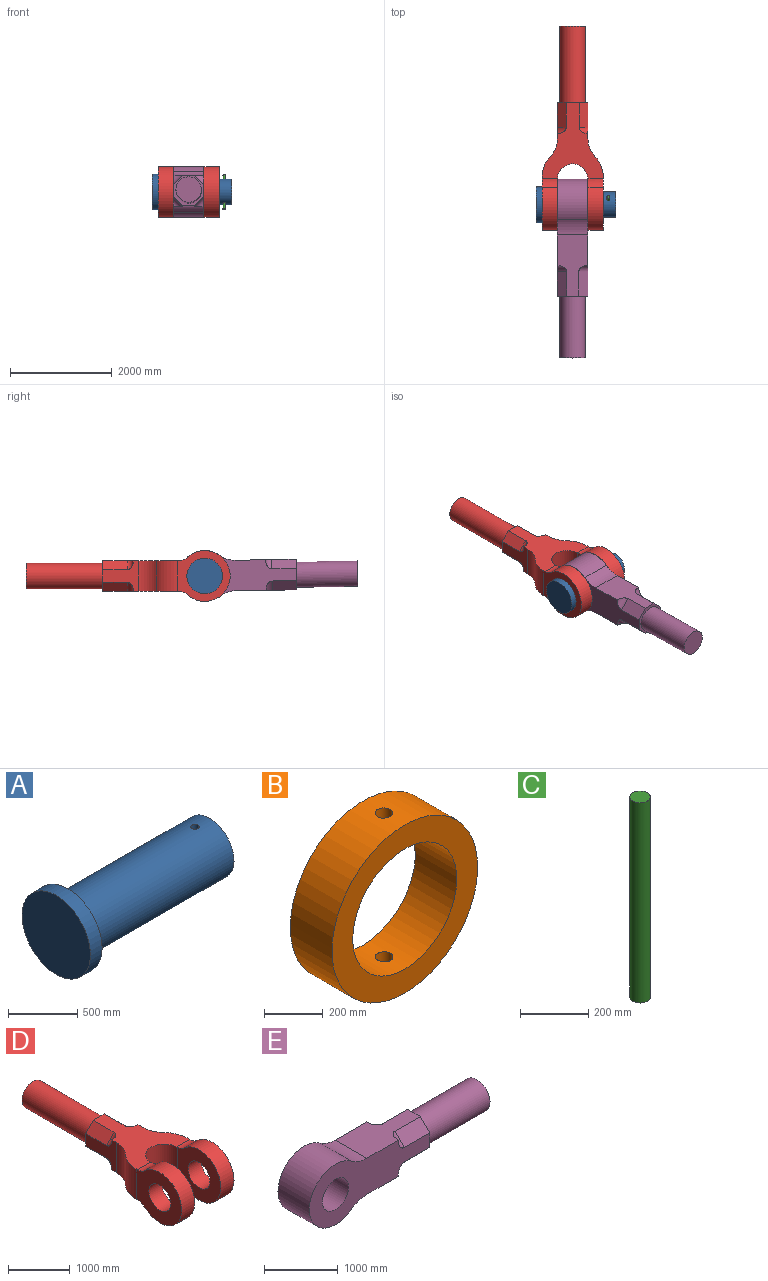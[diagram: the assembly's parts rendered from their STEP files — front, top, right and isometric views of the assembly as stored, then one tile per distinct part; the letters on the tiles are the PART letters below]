
ASSEMBLY  parts=5 mates=5
PART A: 6 faces, bbox 1570x700x700 mm
  f0: cylinder r=250mm len=1450mm, axis (-1,0,0), area 2272006.1mm2, adj f1,f2,f5
  f1: plane 500x500mm, normal (1,0,0), area 196349.5mm2, adj f0
  f2: plane 700x700mm, normal (1,0,0), area 188495.6mm2, adj f0,f3
  f3: cylinder r=350mm len=700mm, axis (-1,0,0), area 263893.8mm2, adj f2,f4
  f4: plane 700x700mm, normal (-1,0,0), area 384845.1mm2, adj f3
  f5: cylinder r=30mm len=500mm, axis (0,0,-1), area 93907.4mm2, adj f0
PART B: 6 faces, bbox 700x200x700 mm
  f0: cylinder r=250mm len=500mm, axis (0,1,0), area 308511.8mm2, adj f2,f3,f4,f5
  f1: cylinder r=350mm len=700mm, axis (0,1,0), area 434178.1mm2, adj f2,f3,f4,f5
  f2: plane 700x700mm, normal (0,-1,0), area 188495.6mm2, adj f0,f1
  f3: plane 700x700mm, normal (0,1,0), area 188495.6mm2, adj f0,f1
  f4: cylinder r=30mm len=101.81mm, axis (0,0,1), area 18898.3mm2, adj f0,f1
  f5: cylinder r=30mm len=101.81mm, axis (0,0,1), area 18898.2mm2, adj f0,f1
PART C: 3 faces, bbox 60x60x720 mm
  f0: cylinder r=30mm len=720mm, axis (0,0,-1), area 135716.8mm2, adj f1,f2
  f1: plane 60x60mm, normal (0,0,1), area 2827.4mm2, adj f0
  f2: plane 60x60mm, normal (0,0,-1), area 2827.4mm2, adj f0
PART D: 36 faces, bbox 1200x4007x1000 mm
  f0: plane 600x600mm, normal (0,1,0), area 103098.5mm2, adj f1,f2,f9,f18,f22,f24,f26,f28
  f1: plane 705.02x600mm, normal (-1,0,0), area 222950.5mm2, adj f0,f2,f7,f18,f24,f25,f26,f27
  f2: plane 1490.1x1200mm, normal (0,0,1), area 810833.6mm2, adj f0,f1,f3,f6,f7,f8,f9,f10
  f3: plane 1040x1000mm, normal (-1,0,0), area 635026.5mm2, adj f2,f6,f13,f15,f17,f18,f21
  f4: plane 1000x1000mm, normal (-1,0,0), area 611025.2mm2, adj f12,f14,f16,f19,f20
  f5: plane 1000x1000mm, normal (1,0,0), area 611025.2mm2, adj f12,f13,f15,f17,f21
  f6: cylinder r=600mm len=600mm, axis (0,0,1), area 272324.3mm2, adj f2,f3,f7,f18
  f7: cylinder r=500mm len=600mm, axis (0,0,1), area 226936.9mm2, adj f1,f2,f6,f18
  f8: cylinder r=600mm len=600mm, axis (0,0,1), area 272324.3mm2, adj f2,f10,f11,f18
  f9: plane 705.02x600mm, normal (1,0,0), area 222950.5mm2, adj f0,f2,f10,f18,f22,f23,f28,f29
  f10: cylinder r=500mm len=600mm, axis (0,0,1), area 226936.9mm2, adj f2,f8,f9,f18
  f11: plane 1040x1000mm, normal (1,0,0), area 635026.5mm2, adj f2,f8,f14,f16,f18,f19,f20
  f12: cylinder r=300mm len=600.39mm, axis (0,0,1), area 565489.3mm2, adj f2,f4,f5,f15,f16,f17,f18,f19
  f13: cylinder r=500mm len=1000mm, axis (1,0,0), area 695514.2mm2, adj f3,f5,f15,f17
  f14: cylinder r=500mm len=1000mm, axis (1,0,0), area 695514.2mm2, adj f4,f11,f16,f19
  f15: cylinder r=250mm len=300.16mm, axis (1,0,0), area 56069.4mm2, adj f2,f3,f5,f12,f13
  f16: cylinder r=250mm len=300.16mm, axis (1,0,0), area 56069.4mm2, adj f2,f4,f11,f12,f14
  f17: cylinder r=250mm len=300.16mm, axis (1,0,0), area 56069.4mm2, adj f3,f5,f12,f13,f18
  f18: plane 1490.1x1200mm, normal (0,0,-1), area 810833.6mm2, adj f0,f1,f3,f6,f7,f8,f9,f10
  f19: cylinder r=250mm len=300.16mm, axis (1,0,0), area 56069.4mm2, adj f4,f11,f12,f14,f18
  f20: cylinder r=250mm len=500mm, axis (1,0,0), area 471238.9mm2, adj f4,f11
  f21: cylinder r=250mm len=500mm, axis (1,0,0), area 471238.9mm2, adj f3,f5
  f22: plane 480x174mm, normal (0.71,0,-0.71), area 118115.1mm2, adj f0,f9,f18,f33
  f23: plane 4.29x4.29mm, normal (0,1,0), area 9.2mm2, adj f9,f18,f33
  f24: plane 480x174mm, normal (-0.71,0,-0.71), area 118115.1mm2, adj f0,f1,f18,f32
  f25: plane 4.29x4.29mm, normal (0,1,0), area 9.2mm2, adj f1,f18,f32
  f26: plane 480x174mm, normal (-0.71,0,0.71), area 118115.1mm2, adj f0,f1,f2,f35
  f27: plane 4.29x4.29mm, normal (0,1,0), area 9.2mm2, adj f1,f2,f35
  f28: plane 480x174mm, normal (0.71,0,0.71), area 118115.1mm2, adj f0,f2,f9,f34
  f29: plane 4.29x4.29mm, normal (0,1,0), area 9.2mm2, adj f2,f9,f34
  f30: cylinder r=250mm len=1507mm, axis (0,-1,0), area 2367190.1mm2, adj f0,f31
  f31: plane 500x500mm, normal (0,1,0), area 196349.5mm2, adj f30
  f32: cylinder r=120mm len=258.85mm, axis (0.71,0,-0.71), area 29944.8mm2, adj f1,f18,f24,f25
  f33: cylinder r=120mm len=258.85mm, axis (0.71,0,0.71), area 29944.8mm2, adj f9,f18,f22,f23
  f34: cylinder r=120mm len=258.85mm, axis (-0.71,0,0.71), area 29944.8mm2, adj f2,f9,f28,f29
  f35: cylinder r=120mm len=258.85mm, axis (-0.71,0,-0.71), area 29944.8mm2, adj f1,f2,f26,f27
PART E: 23 faces, bbox 3505x769.7x1000 mm
  f0: plane 1200x600mm, normal (0,0,1), area 512020.6mm2, adj f2,f3,f6,f8,f9,f10,f13,f14
  f1: plane 1200x600mm, normal (0,0,-1), area 512020.6mm2, adj f2,f5,f6,f8,f11,f12,f15,f16
  f2: plane 2300x1000mm, normal (0,-1,0), area 1188370.1mm2, adj f0,f1,f3,f4,f5,f6,f7,f13
  f3: cylinder r=500mm len=600mm, axis (0,1,0), area 193050.3mm2, adj f0,f2,f4,f8
  f4: cylinder r=500mm len=1000mm, axis (0,1,0), area 1328578.5mm2, adj f2,f3,f5,f8
  f5: cylinder r=500mm len=600mm, axis (0,1,0), area 193050.3mm2, adj f1,f2,f4,f8
  f6: plane 600x600mm, normal (1,0,0), area 98417.7mm2, adj f0,f1,f2,f8,f9,f11,f13,f15
  f7: cylinder r=250mm len=600mm, axis (0,1,0), area 942477.8mm2, adj f2,f8
  f8: plane 2300x1000mm, normal (0,1,0), area 1188370.1mm2, adj f0,f1,f3,f4,f5,f6,f7,f9
  f9: plane 480x180.6mm, normal (0,0.71,0.71), area 122595.3mm2, adj f0,f6,f8,f21
  f10: plane 10.89x10.89mm, normal (1,0,0), area 59.3mm2, adj f0,f8,f21
  f11: plane 480x180.6mm, normal (0,0.71,-0.71), area 122595.3mm2, adj f1,f6,f8,f20
  f12: plane 10.89x10.89mm, normal (1,0,0), area 59.3mm2, adj f1,f8,f20
  f13: plane 480x180.6mm, normal (0,-0.71,0.71), area 122595.3mm2, adj f0,f2,f6,f22
  f14: plane 10.89x10.89mm, normal (1,0,0), area 59.3mm2, adj f0,f2,f22
  f15: plane 480x180.6mm, normal (0,-0.71,-0.71), area 122595.3mm2, adj f1,f2,f6,f19
  f16: plane 10.89x10.89mm, normal (1,0,0), area 59.3mm2, adj f1,f2,f19
  f17: cylinder r=250mm len=1205mm, axis (-1,0,0), area 1892809.6mm2, adj f6,f18
  f18: plane 500x500mm, normal (1,0,0), area 196349.5mm2, adj f17
  f19: cylinder r=120mm len=265.45mm, axis (0,-0.71,0.71), area 31704.1mm2, adj f1,f2,f15,f16
  f20: cylinder r=120mm len=265.45mm, axis (0,-0.71,-0.71), area 31704.1mm2, adj f1,f8,f11,f12
  f21: cylinder r=120mm len=265.45mm, axis (0,0.71,-0.71), area 31704.1mm2, adj f0,f8,f9,f10
  f22: cylinder r=120mm len=265.45mm, axis (0,0.71,0.71), area 31704.1mm2, adj f0,f2,f13,f14
PLACE A rot(axis=(-1,0,0),24.8deg) t=(428.85,-792.19,1431.54)mm
PLACE B rot(axis=(0.7,-0.7,0.15),162.6deg) t=(-396.15,-792.19,1431.54)mm
PLACE C rot(axis=(-1,0,0),24.8deg) t=(278.85,-944.57,1101.01)mm
PLACE D t=(178.85,-1292.19,931.54)mm fixed
PLACE E rot(axis=(-0.01,-0.01,-1),90deg) t=(-121.15,-792.19,1431.54)mm
MATE revolute E.f7 <-> D.f13  axis (1,0,0) through (-121.15,-792.19,1431.54)mm
MATE slider A.f5 <-> C.f0  axis (0,-0.42,-0.91) through (278.85,-686.25,1661.32)mm
MATE cylindrical B.f1 <-> A.f0  axis (1,0,0) through (-196.15,-792.19,1431.54)mm
MATE planar D.f13 <-> A.f0  axis (-1,0,0) through (-1021.15,-792.19,1431.54)mm
MATE cylindrical A.f0 <-> D.f13  axis (-1,0,0) through (428.85,-792.19,1431.54)mm
